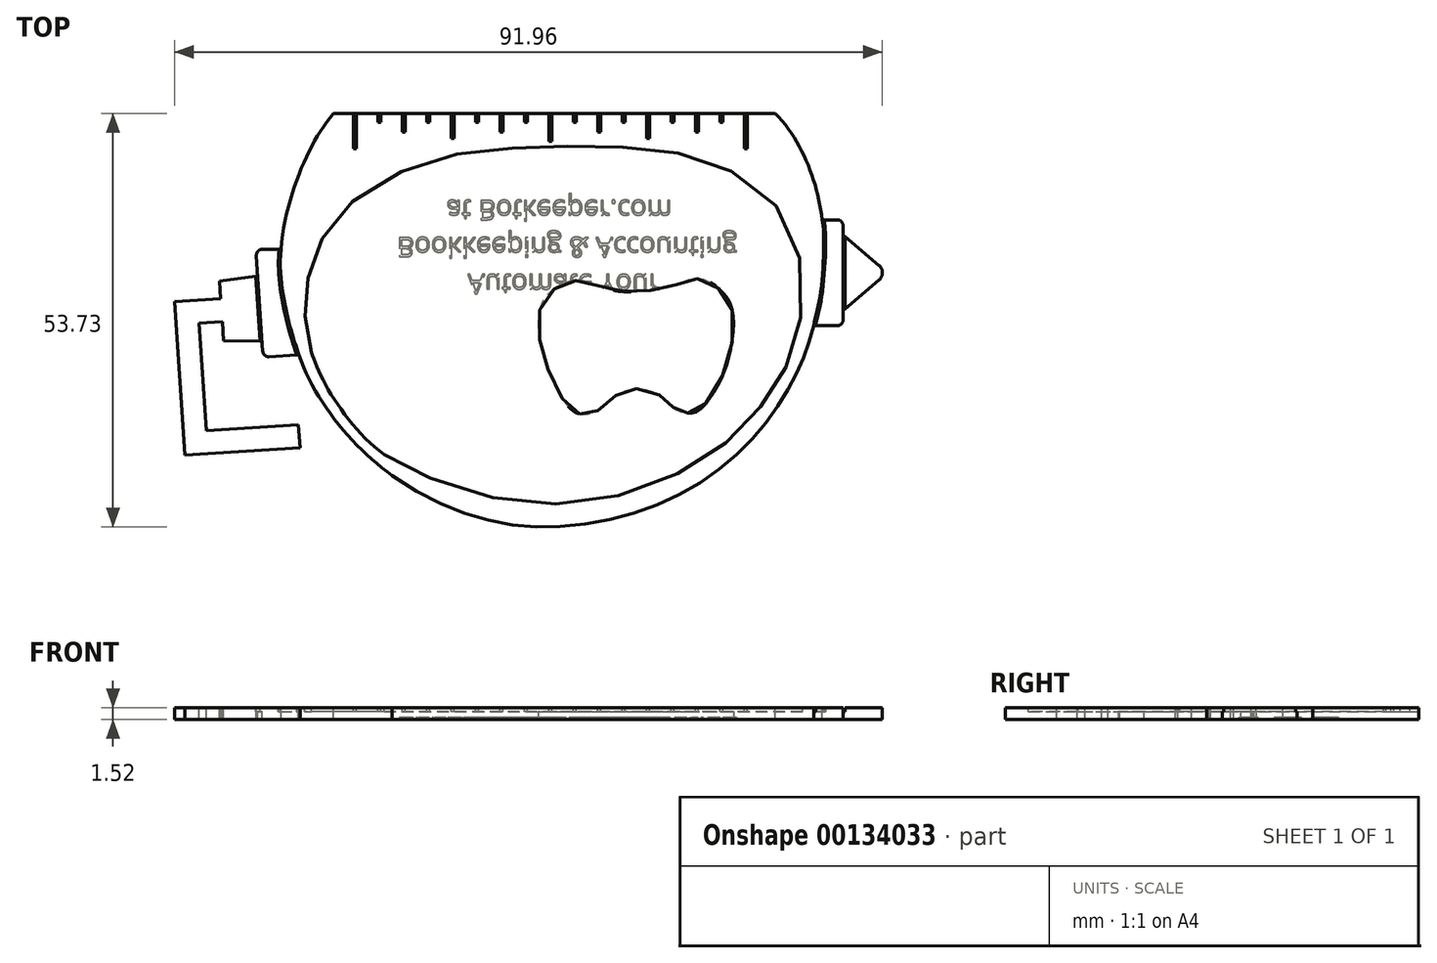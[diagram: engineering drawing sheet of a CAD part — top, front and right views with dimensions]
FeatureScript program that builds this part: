
annotation { "Feature Type Name" : "Feature", "Feature Type Description" : "" }
export const myFeature = defineFeature(function(context is Context, id is Id, definition is map)
    precondition{}
    {
        {
            var Q0;
            Q0=qCreatedBy(makeId("Top.planeOp"),FACE);
            var sketch = newSketch(context, id + "F0", { "sketchPlane" : qUnion([Q0])});
            skLineSegment(sketch, "E0", {"start": v(-32.17, -4.38) * mm, "end": v(25.24, -4.38) * mm});
            skFitSpline(sketch, "E1", {"points": [v(17.6, 42.66) * mm, v(-3.45, 49.33) * mm, v(-23.04, 43.2) * mm, v(-33.77, 31.64) * mm, v(-37.48, 21.94) * mm, v(-38.3, 9.44) * mm, v(-32.1, -4.46) * mm], "startDerivative": vector(-109.73, 76.09) * mm, "endDerivative": vector(66.24, -66.24) * mm});
            skFitSpline(sketch, "E2", {"points": [v(25.23, -4.4) * mm, v(29.6, 3.26) * mm, v(32.13, 15.9) * mm, v(29.75, 26.97) * mm], "startDerivative": vector(17.83, 21.76) * mm, "endDerivative": vector(-8.71, 27.13) * mm});
            skLineSegment(sketch, "E3", {"start": v(32.06, 13.27) * mm, "end": v(35.3, 13.27) * mm});
            skLineSegment(sketch, "E4", {"start": v(35.3, 13.27) * mm, "end": v(34.36, 27.3) * mm});
            skLineSegment(sketch, "E5", {"start": v(34.36, 27.3) * mm, "end": v(29.75, 26.97) * mm});
            skLineSegment(sketch, "E6", {"start": v(34.5, 25.2) * mm, "end": v(39.51, 25.18) * mm});
            skLineSegment(sketch, "E7", {"start": v(39.51, 25.18) * mm, "end": v(40.03, 17.43) * mm});
            skLineSegment(sketch, "E8", {"start": v(40.03, 17.43) * mm, "end": v(35.06, 16.75) * mm});
            skLineSegment(sketch, "E9", {"start": v(-37.18, 23.2) * mm, "end": v(-41, 23.2) * mm});
            skLineSegment(sketch, "E10", {"start": v(-41, 23.2) * mm, "end": v(-41, 9.44) * mm});
            skLineSegment(sketch, "E11", {"start": v(-41, 9.44) * mm, "end": v(-38.3, 9.44) * mm});
            skLineSegment(sketch, "E12", {"start": v(-41, 21.2) * mm, "end": v(-46.8, 16.32) * mm});
            skLineSegment(sketch, "E13", {"start": v(-46.8, 16.32) * mm, "end": v(-41, 11.44) * mm});
            skLineSegment(sketch, "E14.bottom", {"start": v(-28.58, 0.2) * mm, "end": v(-28.2, 0.2) * mm});
            skLineSegment(sketch, "E14.top", {"start": v(-28.58, -4.38) * mm, "end": v(-28.2, -4.38) * mm});
            skLineSegment(sketch, "E14.left", {"start": v(-28.58, 0.2) * mm, "end": v(-28.58, -4.38) * mm});
            skLineSegment(sketch, "E14.right", {"start": v(-28.2, 0.2) * mm, "end": v(-28.2, -4.38) * mm});
            skLineSegment(sketch, "E15.bottom", {"start": v(-25.4, -3.21) * mm, "end": v(-25.02, -3.21) * mm});
            skLineSegment(sketch, "E15.top", {"start": v(-25.4, -4.38) * mm, "end": v(-25.02, -4.38) * mm});
            skLineSegment(sketch, "E15.left", {"start": v(-25.4, -3.21) * mm, "end": v(-25.4, -4.38) * mm});
            skLineSegment(sketch, "E15.right", {"start": v(-25.02, -3.21) * mm, "end": v(-25.02, -4.38) * mm});
            skLineSegment(sketch, "E16.bottom", {"start": v(-22.23, -1.94) * mm, "end": v(-21.84, -1.94) * mm});
            skLineSegment(sketch, "E16.top", {"start": v(-22.23, -4.38) * mm, "end": v(-21.84, -4.38) * mm});
            skLineSegment(sketch, "E16.left", {"start": v(-22.23, -1.94) * mm, "end": v(-22.23, -4.38) * mm});
            skLineSegment(sketch, "E16.right", {"start": v(-21.84, -1.94) * mm, "end": v(-21.84, -4.38) * mm});
            skLineSegment(sketch, "E17.bottom", {"start": v(-19.05, -3.21) * mm, "end": v(-18.67, -3.21) * mm});
            skLineSegment(sketch, "E17.top", {"start": v(-19.05, -4.38) * mm, "end": v(-18.67, -4.38) * mm});
            skLineSegment(sketch, "E17.left", {"start": v(-19.05, -3.21) * mm, "end": v(-19.05, -4.38) * mm});
            skLineSegment(sketch, "E17.right", {"start": v(-18.67, -3.21) * mm, "end": v(-18.67, -4.38) * mm});
            skLineSegment(sketch, "E18.bottom", {"start": v(-15.88, -1.14) * mm, "end": v(-15.5, -1.14) * mm});
            skLineSegment(sketch, "E18.top", {"start": v(-15.88, -4.38) * mm, "end": v(-15.5, -4.38) * mm});
            skLineSegment(sketch, "E18.left", {"start": v(-15.88, -1.14) * mm, "end": v(-15.88, -4.38) * mm});
            skLineSegment(sketch, "E18.right", {"start": v(-15.5, -1.14) * mm, "end": v(-15.5, -4.38) * mm});
            skLineSegment(sketch, "E19.bottom", {"start": v(-12.7, -3.21) * mm, "end": v(-12.32, -3.21) * mm});
            skLineSegment(sketch, "E19.top", {"start": v(-12.7, -4.38) * mm, "end": v(-12.32, -4.38) * mm});
            skLineSegment(sketch, "E19.left", {"start": v(-12.7, -3.21) * mm, "end": v(-12.7, -4.38) * mm});
            skLineSegment(sketch, "E19.right", {"start": v(-12.32, -3.21) * mm, "end": v(-12.32, -4.38) * mm});
            skLineSegment(sketch, "E20.bottom", {"start": v(-9.52, -1.94) * mm, "end": v(-9.14, -1.94) * mm});
            skLineSegment(sketch, "E20.top", {"start": v(-9.52, -4.38) * mm, "end": v(-9.14, -4.38) * mm});
            skLineSegment(sketch, "E20.left", {"start": v(-9.52, -1.94) * mm, "end": v(-9.52, -4.38) * mm});
            skLineSegment(sketch, "E20.right", {"start": v(-9.14, -1.94) * mm, "end": v(-9.14, -4.38) * mm});
            skLineSegment(sketch, "E21.bottom", {"start": v(-6.35, -3.21) * mm, "end": v(-5.97, -3.21) * mm});
            skLineSegment(sketch, "E21.top", {"start": v(-6.35, -4.38) * mm, "end": v(-5.97, -4.38) * mm});
            skLineSegment(sketch, "E21.left", {"start": v(-6.35, -3.21) * mm, "end": v(-6.35, -4.38) * mm});
            skLineSegment(sketch, "E21.right", {"start": v(-5.97, -3.21) * mm, "end": v(-5.97, -4.38) * mm});
            skLineSegment(sketch, "E22.bottom", {"start": v(-3.18, -0.76) * mm, "end": v(-2.8, -0.76) * mm});
            skLineSegment(sketch, "E22.top", {"start": v(-3.18, -4.38) * mm, "end": v(-2.8, -4.38) * mm});
            skLineSegment(sketch, "E22.left", {"start": v(-3.18, -0.76) * mm, "end": v(-3.18, -4.38) * mm});
            skLineSegment(sketch, "E22.right", {"start": v(-2.8, -0.76) * mm, "end": v(-2.8, -4.38) * mm});
            skLineSegment(sketch, "E23.bottom", {"start": v(0, -3.21) * mm, "end": v(0.38, -3.21) * mm});
            skLineSegment(sketch, "E23.top", {"start": v(0, -4.38) * mm, "end": v(0.38, -4.38) * mm});
            skLineSegment(sketch, "E23.left", {"start": v(0, -3.21) * mm, "end": v(0, -4.38) * mm});
            skLineSegment(sketch, "E23.right", {"start": v(0.38, -3.21) * mm, "end": v(0.38, -4.38) * mm});
            skLineSegment(sketch, "E24.bottom", {"start": v(3.18, -1.94) * mm, "end": v(3.56, -1.94) * mm});
            skLineSegment(sketch, "E24.top", {"start": v(3.18, -4.38) * mm, "end": v(3.56, -4.38) * mm});
            skLineSegment(sketch, "E24.left", {"start": v(3.18, -1.94) * mm, "end": v(3.18, -4.38) * mm});
            skLineSegment(sketch, "E24.right", {"start": v(3.56, -1.94) * mm, "end": v(3.56, -4.38) * mm});
            skLineSegment(sketch, "E25.bottom", {"start": v(6.35, -3.21) * mm, "end": v(6.73, -3.21) * mm});
            skLineSegment(sketch, "E25.top", {"start": v(6.35, -4.38) * mm, "end": v(6.73, -4.38) * mm});
            skLineSegment(sketch, "E25.left", {"start": v(6.35, -3.21) * mm, "end": v(6.35, -4.38) * mm});
            skLineSegment(sketch, "E25.right", {"start": v(6.73, -3.21) * mm, "end": v(6.73, -4.38) * mm});
            skLineSegment(sketch, "E26.bottom", {"start": v(9.52, -1.14) * mm, "end": v(9.9, -1.14) * mm});
            skLineSegment(sketch, "E26.top", {"start": v(9.52, -4.38) * mm, "end": v(9.9, -4.38) * mm});
            skLineSegment(sketch, "E26.left", {"start": v(9.52, -1.14) * mm, "end": v(9.52, -4.38) * mm});
            skLineSegment(sketch, "E26.right", {"start": v(9.9, -1.14) * mm, "end": v(9.9, -4.38) * mm});
            skLineSegment(sketch, "E27.bottom", {"start": v(12.7, -3.21) * mm, "end": v(13.08, -3.21) * mm});
            skLineSegment(sketch, "E27.top", {"start": v(12.7, -4.38) * mm, "end": v(13.08, -4.38) * mm});
            skLineSegment(sketch, "E27.left", {"start": v(12.7, -3.21) * mm, "end": v(12.7, -4.38) * mm});
            skLineSegment(sketch, "E27.right", {"start": v(13.08, -3.21) * mm, "end": v(13.08, -4.38) * mm});
            skLineSegment(sketch, "E28.bottom", {"start": v(15.88, -1.94) * mm, "end": v(16.26, -1.94) * mm});
            skLineSegment(sketch, "E28.top", {"start": v(15.88, -4.38) * mm, "end": v(16.26, -4.38) * mm});
            skLineSegment(sketch, "E28.left", {"start": v(15.88, -1.94) * mm, "end": v(15.88, -4.38) * mm});
            skLineSegment(sketch, "E28.right", {"start": v(16.26, -1.94) * mm, "end": v(16.26, -4.38) * mm});
            skLineSegment(sketch, "E29.bottom", {"start": v(19.05, -3.21) * mm, "end": v(19.43, -3.21) * mm});
            skLineSegment(sketch, "E29.top", {"start": v(19.05, -4.38) * mm, "end": v(19.43, -4.38) * mm});
            skLineSegment(sketch, "E29.left", {"start": v(19.05, -3.21) * mm, "end": v(19.05, -4.38) * mm});
            skLineSegment(sketch, "E29.right", {"start": v(19.43, -3.21) * mm, "end": v(19.43, -4.38) * mm});
            skLineSegment(sketch, "E30.bottom", {"start": v(22.23, 0.2) * mm, "end": v(22.6, 0.2) * mm});
            skLineSegment(sketch, "E30.top", {"start": v(22.23, -4.38) * mm, "end": v(22.6, -4.38) * mm});
            skLineSegment(sketch, "E30.left", {"start": v(22.23, 0.2) * mm, "end": v(22.23, -4.38) * mm});
            skLineSegment(sketch, "E30.right", {"start": v(22.6, 0.2) * mm, "end": v(22.6, -4.38) * mm});
            skFitSpline(sketch, "E31", {"points": [v(29.75, 26.97) * mm, v(17.6, 42.66) * mm], "startDerivative": vector(-6.37, 18.37) * mm, "endDerivative": vector(-15.48, 11.18) * mm});
            skSolve(sketch);
        }
        {
            var Q0;
            {var subQ0=sQuery(id+"F0.wireOp",EDGE,"E12");Q0=makeQuery(id+"F0.imprint","IMPRINT",FACE,{"disambiguationData":[TD([[makeQuery(id+"F0.imprint","IMPRINT",EDGE,{"derivedFrom":subQ0}),1.0]])]});}
            var Q1;
            {var subQ0=sQuery(id+"F0.wireOp",EDGE,"E9");Q1=makeQuery(id+"F0.imprint","IMPRINT",FACE,{"disambiguationData":[TD([[makeQuery(id+"F0.imprint","IMPRINT",EDGE,{"derivedFrom":subQ0}),1.0]])]});}
            var Q2;
            {var subQ4=sQuery(id+"F0.wireOp",EDGE,"E0");Q2=makeQuery(id+"F0.imprint","IMPRINT",FACE,{"disambiguationData":[TD([[makeQuery(id+"F0.imprint","IMPRINT",EDGE,{"derivedFrom":subQ4}),1.0]])]});}
            var Q3;
            {var subQ3=sQuery(id+"F0.wireOp",EDGE,"E3");Q3=makeQuery(id+"F0.imprint","IMPRINT",FACE,{"disambiguationData":[TD([[makeQuery(id+"F0.imprint","IMPRINT",EDGE,{"derivedFrom":subQ3}),1.0]])]});}
            var Q4;
            {var subQ0=sQuery(id+"F0.wireOp",EDGE,"E6");Q4=makeQuery(id+"F0.imprint","IMPRINT",FACE,{"disambiguationData":[TD([[makeQuery(id+"F0.imprint","IMPRINT",EDGE,{"derivedFrom":subQ0}),-1.0]])]});}
            var Q5;
            Q5=makeQuery(id+"F0.imprint","IMPRINT",FACE,{"disambiguationData":[TD([[makeQuery(id+"F0.imprint","IMPRINT",EDGE,{"derivedFrom":sQuery(id+"F0.wireOp",EDGE,"E14.bottom")}),-1.0]])]});
            var Q6;
            Q6=makeQuery(id+"F0.imprint","IMPRINT",FACE,{"disambiguationData":[TD([[makeQuery(id+"F0.imprint","IMPRINT",EDGE,{"derivedFrom":sQuery(id+"F0.wireOp",EDGE,"E15.bottom")}),-1.0]])]});
            var Q7;
            Q7=makeQuery(id+"F0.imprint","IMPRINT",FACE,{"disambiguationData":[TD([[makeQuery(id+"F0.imprint","IMPRINT",EDGE,{"derivedFrom":sQuery(id+"F0.wireOp",EDGE,"E16.bottom")}),-1.0]])]});
            var Q8;
            Q8=makeQuery(id+"F0.imprint","IMPRINT",FACE,{"disambiguationData":[TD([[makeQuery(id+"F0.imprint","IMPRINT",EDGE,{"derivedFrom":sQuery(id+"F0.wireOp",EDGE,"E17.bottom")}),-1.0]])]});
            var Q9;
            Q9=makeQuery(id+"F0.imprint","IMPRINT",FACE,{"disambiguationData":[TD([[makeQuery(id+"F0.imprint","IMPRINT",EDGE,{"derivedFrom":sQuery(id+"F0.wireOp",EDGE,"E18.bottom")}),-1.0]])]});
            var Q10;
            Q10=makeQuery(id+"F0.imprint","IMPRINT",FACE,{"disambiguationData":[TD([[makeQuery(id+"F0.imprint","IMPRINT",EDGE,{"derivedFrom":sQuery(id+"F0.wireOp",EDGE,"E19.bottom")}),-1.0]])]});
            var Q11;
            Q11=makeQuery(id+"F0.imprint","IMPRINT",FACE,{"disambiguationData":[TD([[makeQuery(id+"F0.imprint","IMPRINT",EDGE,{"derivedFrom":sQuery(id+"F0.wireOp",EDGE,"E20.bottom")}),-1.0]])]});
            var Q12;
            Q12=makeQuery(id+"F0.imprint","IMPRINT",FACE,{"disambiguationData":[TD([[makeQuery(id+"F0.imprint","IMPRINT",EDGE,{"derivedFrom":sQuery(id+"F0.wireOp",EDGE,"E21.bottom")}),-1.0]])]});
            var Q13;
            Q13=makeQuery(id+"F0.imprint","IMPRINT",FACE,{"disambiguationData":[TD([[makeQuery(id+"F0.imprint","IMPRINT",EDGE,{"derivedFrom":sQuery(id+"F0.wireOp",EDGE,"E22.bottom")}),-1.0]])]});
            var Q14;
            Q14=makeQuery(id+"F0.imprint","IMPRINT",FACE,{"disambiguationData":[TD([[makeQuery(id+"F0.imprint","IMPRINT",EDGE,{"derivedFrom":sQuery(id+"F0.wireOp",EDGE,"E23.bottom")}),-1.0]])]});
            var Q15;
            Q15=makeQuery(id+"F0.imprint","IMPRINT",FACE,{"disambiguationData":[TD([[makeQuery(id+"F0.imprint","IMPRINT",EDGE,{"derivedFrom":sQuery(id+"F0.wireOp",EDGE,"E24.bottom")}),-1.0]])]});
            var Q16;
            Q16=makeQuery(id+"F0.imprint","IMPRINT",FACE,{"disambiguationData":[TD([[makeQuery(id+"F0.imprint","IMPRINT",EDGE,{"derivedFrom":sQuery(id+"F0.wireOp",EDGE,"E25.bottom")}),-1.0]])]});
            var Q17;
            Q17=makeQuery(id+"F0.imprint","IMPRINT",FACE,{"disambiguationData":[TD([[makeQuery(id+"F0.imprint","IMPRINT",EDGE,{"derivedFrom":sQuery(id+"F0.wireOp",EDGE,"E26.bottom")}),-1.0]])]});
            var Q18;
            Q18=makeQuery(id+"F0.imprint","IMPRINT",FACE,{"disambiguationData":[TD([[makeQuery(id+"F0.imprint","IMPRINT",EDGE,{"derivedFrom":sQuery(id+"F0.wireOp",EDGE,"E27.bottom")}),-1.0]])]});
            var Q19;
            Q19=makeQuery(id+"F0.imprint","IMPRINT",FACE,{"disambiguationData":[TD([[makeQuery(id+"F0.imprint","IMPRINT",EDGE,{"derivedFrom":sQuery(id+"F0.wireOp",EDGE,"E28.bottom")}),-1.0]])]});
            var Q20;
            Q20=makeQuery(id+"F0.imprint","IMPRINT",FACE,{"disambiguationData":[TD([[makeQuery(id+"F0.imprint","IMPRINT",EDGE,{"derivedFrom":sQuery(id+"F0.wireOp",EDGE,"E29.bottom")}),-1.0]])]});
            var Q21;
            Q21=makeQuery(id+"F0.imprint","IMPRINT",FACE,{"disambiguationData":[TD([[makeQuery(id+"F0.imprint","IMPRINT",EDGE,{"derivedFrom":sQuery(id+"F0.wireOp",EDGE,"E30.bottom")}),-1.0]])]});
            extrude(context, id + "F1", {"entities" : qUnion([Q0, Q1, Q2, Q3, Q4, Q5, Q6, Q7, Q8, Q9, Q10, Q11, Q12, Q13, Q14, Q15, Q16, Q17, Q18, Q19, Q20, Q21]), "oppositeDirection" : true, "depth" : 1.52 * mm});
        }
        {
            var Q0;
            Q0=makeQuery(id+"F0.imprint","IMPRINT",FACE,{"disambiguationData":[TD([[makeQuery(id+"F0.imprint","IMPRINT",EDGE,{"derivedFrom":sQuery(id+"F0.wireOp",EDGE,"E14.bottom")}),1.0]])]});
            var sketch = newSketch(context, id + "F2", { "sketchPlane" : qUnion([Q0])});
            skCircle(sketch, "E32", {"center": v(-14.4, 25.5) * mm, "radius": 6.39 * mm, "construction": true});
            skPoint(sketch, "E32.first.point", {"position": v(-19.79, 28.93) * mm});
            skPoint(sketch, "E32.second.point", {"position": v(-8.02, 25.7) * mm});
            skPoint(sketch, "E32.third.point", {"position": v(-14.79, 19.13) * mm});
            skCircle(sketch, "E33", {"center": v(-14.4, 25.5) * mm, "radius": 8.66 * mm, "construction": true});
            skPoint(sketch, "E33.first.point", {"position": v(-17.82, 33.46) * mm});
            skPoint(sketch, "E33.second.point", {"position": v(-5.87, 27.02) * mm});
            skPoint(sketch, "E33.third.point", {"position": v(-19.38, 18.42) * mm});
            skArc(sketch, "E34", {"start": v(13.5, 25.47) * mm, "mid": v(7.55, 27.76) * mm, "end": v(1.85, 24.89) * mm});
            skArc(sketch, "E35", {"start": v(15.13, 27.13) * mm, "mid": v(7.4, 30.06) * mm, "end": v(-0.06, 26.51) * mm});
            skArc(sketch, "E36", {"start": v(-0.06, 26.51) * mm, "mid": v(0.07, 24.73) * mm, "end": v(1.85, 24.89) * mm});
            skArc(sketch, "E37", {"start": v(13.5, 25.47) * mm, "mid": v(15.16, 25.47) * mm, "end": v(15.13, 27.13) * mm});
            skArc(sketch, "E38", {"start": v(-11.18, 12.88) * mm, "mid": v(-2.27, 11.02) * mm, "end": v(5.19, 16.23) * mm});
            skArc(sketch, "E39", {"start": v(-12.5, 11) * mm, "mid": v(-1.88, 8.77) * mm, "end": v(7.06, 14.9) * mm});
            skArc(sketch, "E40", {"start": v(-11.18, 12.88) * mm, "mid": v(-12.77, 12.6) * mm, "end": v(-12.5, 11) * mm});
            skLineSegment(sketch, "E41", {"start": v(5.19, 16.23) * mm, "end": v(4.3, 16.9) * mm});
            skLineSegment(sketch, "E42", {"start": v(7.06, 14.9) * mm, "end": v(7.66, 14.46) * mm});
            skLineSegment(sketch, "E43", {"start": v(5.65, 18.78) * mm, "end": v(9.06, 16.4) * mm});
            skArc(sketch, "E44", {"start": v(5.65, 18.78) * mm, "mid": v(4.05, 18.51) * mm, "end": v(4.3, 16.9) * mm});
            skArc(sketch, "E45", {"start": v(7.66, 14.46) * mm, "mid": v(9.34, 14.72) * mm, "end": v(9.06, 16.4) * mm});
            skPoint(sketch, "E46.first.point", {"position": v(-14.74, 32.09) * mm});
            skPoint(sketch, "E46.second.point", {"position": v(-20.28, 23.46) * mm});
            skPoint(sketch, "E46.third.point", {"position": v(-8.39, 22.95) * mm});
            skSolve(sketch);
        }
        {
            var Q0;
            Q0 = qSketchRegion(id + "F2", true);
            extrude(context, id + "F3", {"entities" : qUnion([Q0]), "operationType" : NewBodyOperationType.REMOVE, "oppositeDirection" : true, "depth" : 0.5 * mm});
        }
        {
            var Q0;
            Q0=makeQuery(id+"F0.imprint","IMPRINT",FACE,{"disambiguationData":[TD([[makeQuery(id+"F0.imprint","IMPRINT",EDGE,{"derivedFrom":sQuery(id+"F0.wireOp",EDGE,"E14.bottom")}),-1.0]])]});
            var Q1;
            Q1=makeQuery(id+"F0.imprint","IMPRINT",FACE,{"disambiguationData":[TD([[makeQuery(id+"F0.imprint","IMPRINT",EDGE,{"derivedFrom":sQuery(id+"F0.wireOp",EDGE,"E15.bottom")}),-1.0]])]});
            var Q2;
            Q2=makeQuery(id+"F0.imprint","IMPRINT",FACE,{"disambiguationData":[TD([[makeQuery(id+"F0.imprint","IMPRINT",EDGE,{"derivedFrom":sQuery(id+"F0.wireOp",EDGE,"E16.bottom")}),-1.0]])]});
            var Q3;
            Q3=makeQuery(id+"F0.imprint","IMPRINT",FACE,{"disambiguationData":[TD([[makeQuery(id+"F0.imprint","IMPRINT",EDGE,{"derivedFrom":sQuery(id+"F0.wireOp",EDGE,"E18.bottom")}),-1.0]])]});
            var Q4;
            Q4=makeQuery(id+"F0.imprint","IMPRINT",FACE,{"disambiguationData":[TD([[makeQuery(id+"F0.imprint","IMPRINT",EDGE,{"derivedFrom":sQuery(id+"F0.wireOp",EDGE,"E17.bottom")}),-1.0]])]});
            var Q5;
            Q5=makeQuery(id+"F0.imprint","IMPRINT",FACE,{"disambiguationData":[TD([[makeQuery(id+"F0.imprint","IMPRINT",EDGE,{"derivedFrom":sQuery(id+"F0.wireOp",EDGE,"E19.bottom")}),-1.0]])]});
            var Q6;
            Q6=makeQuery(id+"F0.imprint","IMPRINT",FACE,{"disambiguationData":[TD([[makeQuery(id+"F0.imprint","IMPRINT",EDGE,{"derivedFrom":sQuery(id+"F0.wireOp",EDGE,"E20.bottom")}),-1.0]])]});
            var Q7;
            Q7=makeQuery(id+"F0.imprint","IMPRINT",FACE,{"disambiguationData":[TD([[makeQuery(id+"F0.imprint","IMPRINT",EDGE,{"derivedFrom":sQuery(id+"F0.wireOp",EDGE,"E21.bottom")}),-1.0]])]});
            var Q8;
            Q8=makeQuery(id+"F0.imprint","IMPRINT",FACE,{"disambiguationData":[TD([[makeQuery(id+"F0.imprint","IMPRINT",EDGE,{"derivedFrom":sQuery(id+"F0.wireOp",EDGE,"E22.bottom")}),-1.0]])]});
            var Q9;
            Q9=makeQuery(id+"F0.imprint","IMPRINT",FACE,{"disambiguationData":[TD([[makeQuery(id+"F0.imprint","IMPRINT",EDGE,{"derivedFrom":sQuery(id+"F0.wireOp",EDGE,"E23.bottom")}),-1.0]])]});
            var Q10;
            Q10=makeQuery(id+"F0.imprint","IMPRINT",FACE,{"disambiguationData":[TD([[makeQuery(id+"F0.imprint","IMPRINT",EDGE,{"derivedFrom":sQuery(id+"F0.wireOp",EDGE,"E24.bottom")}),-1.0]])]});
            var Q11;
            Q11=makeQuery(id+"F0.imprint","IMPRINT",FACE,{"disambiguationData":[TD([[makeQuery(id+"F0.imprint","IMPRINT",EDGE,{"derivedFrom":sQuery(id+"F0.wireOp",EDGE,"E25.bottom")}),-1.0]])]});
            var Q12;
            Q12=makeQuery(id+"F0.imprint","IMPRINT",FACE,{"disambiguationData":[TD([[makeQuery(id+"F0.imprint","IMPRINT",EDGE,{"derivedFrom":sQuery(id+"F0.wireOp",EDGE,"E26.bottom")}),-1.0]])]});
            var Q13;
            Q13=makeQuery(id+"F0.imprint","IMPRINT",FACE,{"disambiguationData":[TD([[makeQuery(id+"F0.imprint","IMPRINT",EDGE,{"derivedFrom":sQuery(id+"F0.wireOp",EDGE,"E27.bottom")}),-1.0]])]});
            var Q14;
            Q14=makeQuery(id+"F0.imprint","IMPRINT",FACE,{"disambiguationData":[TD([[makeQuery(id+"F0.imprint","IMPRINT",EDGE,{"derivedFrom":sQuery(id+"F0.wireOp",EDGE,"E28.bottom")}),-1.0]])]});
            var Q15;
            Q15=makeQuery(id+"F0.imprint","IMPRINT",FACE,{"disambiguationData":[TD([[makeQuery(id+"F0.imprint","IMPRINT",EDGE,{"derivedFrom":sQuery(id+"F0.wireOp",EDGE,"E29.bottom")}),-1.0]])]});
            var Q16;
            Q16=makeQuery(id+"F0.imprint","IMPRINT",FACE,{"disambiguationData":[TD([[makeQuery(id+"F0.imprint","IMPRINT",EDGE,{"derivedFrom":sQuery(id+"F0.wireOp",EDGE,"E30.bottom")}),-1.0]])]});
            extrude(context, id + "F4", {"entities" : qUnion([Q0, Q1, Q2, Q3, Q4, Q5, Q6, Q7, Q8, Q9, Q10, Q11, Q12, Q13, Q14, Q15, Q16]), "operationType" : NewBodyOperationType.REMOVE, "oppositeDirection" : true, "depth" : 0.5 * mm});
        }
        {
            var Q0;
            {var subQ0=sQuery(id+"F0.wireOp",EDGE,"E31");var subQ1=sQuery(id+"F0.wireOp",EDGE,"E13");var subQ2=sQuery(id+"F0.wireOp",EDGE,"E12");var subQ3=sQuery(id+"F0.wireOp",EDGE,"E11");var subQ4=sQuery(id+"F0.wireOp",EDGE,"E10");var subQ5=sQuery(id+"F0.wireOp",EDGE,"E9");var subQ6=sQuery(id+"F0.wireOp",EDGE,"E8");var subQ7=sQuery(id+"F0.wireOp",EDGE,"E2");var subQ8=sQuery(id+"F0.wireOp",EDGE,"E1");var subQ9=sQuery(id+"F0.wireOp",EDGE,"E0");var subQ10=sQuery(id+"F0.wireOp",EDGE,"E30.top");var subQ11=sQuery(id+"F0.wireOp",EDGE,"E29.top");var subQ12=sQuery(id+"F0.wireOp",EDGE,"E28.top");var subQ13=sQuery(id+"F0.wireOp",EDGE,"E27.top");var subQ14=sQuery(id+"F0.wireOp",EDGE,"E26.top");var subQ15=sQuery(id+"F0.wireOp",EDGE,"E25.top");var subQ16=sQuery(id+"F0.wireOp",EDGE,"E24.top");var subQ17=sQuery(id+"F0.wireOp",EDGE,"E23.top");var subQ18=sQuery(id+"F0.wireOp",EDGE,"E22.top");var subQ19=sQuery(id+"F0.wireOp",EDGE,"E21.top");var subQ20=sQuery(id+"F0.wireOp",EDGE,"E20.top");var subQ21=sQuery(id+"F0.wireOp",EDGE,"E19.top");var subQ22=sQuery(id+"F0.wireOp",EDGE,"E18.top");var subQ23=sQuery(id+"F0.wireOp",EDGE,"E17.top");var subQ24=sQuery(id+"F0.wireOp",EDGE,"E16.top");var subQ25=sQuery(id+"F0.wireOp",EDGE,"E15.top");var subQ26=sQuery(id+"F0.wireOp",EDGE,"E14.top");var subQ27=sQuery(id+"F0.wireOp",EDGE,"E3");var subQ28=sQuery(id+"F0.wireOp",EDGE,"E4");var subQ29=sQuery(id+"F0.wireOp",EDGE,"E5");var subQ30=sQuery(id+"F0.wireOp",EDGE,"E6");var subQ31=sQuery(id+"F0.wireOp",EDGE,"E7");Q0=makeQuery(id+"F3.boolean.opBoolean","SPLIT",FACE,{"disambiguationData":[TD([makeQuery(id+"F1.opExtrude","SWEPT_FACE",FACE,{"disambiguationData":[OSD([subQ7])]})])],"derivedFrom":makeQuery(id+"F1.opExtrude","CAP_FACE",FACE,{"disambiguationData":[OSD([subQ9,subQ8,subQ7,subQ27,subQ28,subQ29,subQ30,subQ31,subQ6,subQ5,subQ4,subQ3,subQ2,subQ1,subQ26,subQ25,subQ24,subQ23,subQ22,subQ21,subQ20,subQ19,subQ18,subQ17,subQ16,subQ15,subQ14,subQ13,subQ12,subQ11,subQ10,subQ0])],"isStart":true})});}
            var sketch = newSketch(context, id + "F5", { "sketchPlane" : qUnion([Q0])});
            skFitSpline(sketch, "E47", {"points": [v(18.63, 39.92) * mm, v(6.25, 45.15) * mm, v(-9.8, 45.73) * mm, v(-23.9, 39.86) * mm, v(-31.2, 32.51) * mm, v(-35.12, 23.96) * mm, v(-34.08, 10.46) * mm, v(-24.53, 2.23) * mm, v(-12.25, 0) * mm, v(0.1, 0.07) * mm, v(12.6, 1.76) * mm, v(23.95, 8.14) * mm, v(28.06, 15.22) * mm, v(28.98, 21.31) * mm, v(28.06, 26.68) * mm], "startDerivative": vector(-92.5, 61.42) * mm, "endDerivative": vector(-25.36, 109.51) * mm});
            skFitSpline(sketch, "E48.0", {"points": [v(18.77, 40.14) * mm, v(17.8, 40.79) * mm, v(15.7, 41.93) * mm, v(12.18, 43.46) * mm, v(9.3, 44.53) * mm, v(6.3, 45.44) * mm, v(3.3, 46.1) * mm, v(0.33, 46.51) * mm, v(-2.63, 46.68) * mm, v(-5.58, 46.59) * mm, v(-8.52, 46.25) * mm, v(-11.45, 45.66) * mm, v(-15.31, 44.56) * mm, v(-19, 43.05) * mm, v(-22.32, 41.23) * mm, v(-24.57, 39.74) * mm, v(-26.56, 38.15) * mm, v(-28.3, 36.48) * mm, v(-29.85, 34.74) * mm, v(-31.22, 32.96) * mm, v(-32.46, 31.13) * mm, v(-33.55, 29.22) * mm, v(-34.48, 27.16) * mm, v(-35.09, 25.27) * mm, v(-35.47, 23.62) * mm, v(-35.77, 21.88) * mm, v(-36, 19.58) * mm, v(-35.96, 16.72) * mm, v(-35.57, 13.89) * mm, v(-34.9, 11.64) * mm, v(-34.15, 9.97) * mm, v(-33.23, 8.4) * mm, v(-31.82, 6.64) * mm, v(-29.8, 4.84) * mm, v(-27.53, 3.34) * mm, v(-25.1, 2.14) * mm, v(-22.6, 1.23) * mm, v(-20.05, 0.59) * mm, v(-17.46, 0.15) * mm, v(-14.86, -0.12) * mm, v(-12.26, -0.27) * mm, v(-9.66, -0.35) * mm, v(-7.08, -0.37) * mm, v(-4.5, -0.33) * mm, v(-1.91, -0.26) * mm, v(0.66, -0.16) * mm, v(3.24, -0.04) * mm, v(5.82, 0.17) * mm, v(8.42, 0.5) * mm, v(10.6, 0.94) * mm, v(12.34, 1.4) * mm, v(14.1, 1.95) * mm, v(16.28, 2.8) * mm, v(18.8, 4.03) * mm, v(21.13, 5.45) * mm, v(22.86, 6.76) * mm, v(24.07, 7.89) * mm, v(25.15, 9.05) * mm, v(26.27, 10.56) * mm, v(27.3, 12.43) * mm, v(28.06, 14.32) * mm, v(28.64, 16.2) * mm, v(29.04, 18.05) * mm, v(29.25, 19.87) * mm, v(29.25, 21.65) * mm, v(29.05, 23.36) * mm, v(28.71, 25.04) * mm, v(28.44, 26.17) * mm, v(28.31, 26.74) * mm]});
            skFitSpline(sketch, "E49", {"points": [v(16.65, 38.55) * mm, v(8.91, 42.59) * mm, v(-6.12, 44.42) * mm, v(-21.45, 39.35) * mm, v(-32.5, 24.95) * mm, v(-28.84, 9.66) * mm, v(-16.86, 4.32) * mm, v(-0.56, 3.68) * mm, v(17, 7.95) * mm, v(23.1, 12.81) * mm, v(25.48, 18.24) * mm, v(25.01, 25.93) * mm], "startDerivative": vector(-89.1, 67.64) * mm, "endDerivative": vector(-21.26, 103.14) * mm});
            skFitSpline(sketch, "E50.0", {"points": [v(16.5, 38.35) * mm, v(15.57, 39.05) * mm, v(14.17, 40) * mm, v(12.11, 41.08) * mm, v(10.43, 41.8) * mm, v(8.57, 42.45) * mm, v(6.5, 43.03) * mm, v(4.26, 43.5) * mm, v(1.9, 43.88) * mm, v(-0.56, 44.14) * mm, v(-3.05, 44.25) * mm, v(-5.54, 44.22) * mm, v(-8, 44.02) * mm, v(-10.4, 43.65) * mm, v(-13.53, 42.92) * mm, v(-16.58, 41.8) * mm, v(-19.53, 40.28) * mm, v(-22.41, 38.47) * mm, v(-25.89, 35.67) * mm, v(-28.83, 32.27) * mm, v(-30.65, 29.28) * mm, v(-31.71, 26.91) * mm, v(-32.4, 24.45) * mm, v(-32.7, 21.9) * mm, v(-32.63, 19.33) * mm, v(-32.22, 16.82) * mm, v(-31.48, 14.43) * mm, v(-30.45, 12.24) * mm, v(-29.16, 10.32) * mm, v(-27.63, 8.74) * mm, v(-25.88, 7.48) * mm, v(-23.96, 6.48) * mm, v(-21.88, 5.71) * mm, v(-19.7, 5.12) * mm, v(-17.43, 4.66) * mm, v(-15.13, 4.28) * mm, v(-12.8, 3.99) * mm, v(-9.62, 3.7) * mm, v(-5.53, 3.59) * mm, v(-0.35, 3.88) * mm, v(5.16, 4.65) * mm, v(9.64, 5.63) * mm, v(12.93, 6.6) * mm, v(15.2, 7.4) * mm, v(17.19, 8.29) * mm, v(18.87, 9.23) * mm, v(20.3, 10.24) * mm, v(21.5, 11.3) * mm, v(22.51, 12.43) * mm, v(23.4, 13.6) * mm, v(24.13, 14.85) * mm, v(24.72, 16.17) * mm, v(25.07, 17.35) * mm, v(25.25, 18.36) * mm, v(25.37, 19.41) * mm, v(25.4, 20.8) * mm, v(25.27, 23.1) * mm, v(24.99, 24.8) * mm, v(24.77, 25.88) * mm]});
            skFitSpline(sketch, "E51", {"points": [v(18.55, 40.28) * mm, v(28.31, 26.74) * mm], "startDerivative": vector(16.28, -10.65) * mm, "endDerivative": vector(1.29, -6.83) * mm});
            skFitSpline(sketch, "E52", {"points": [v(18.63, 39.92) * mm, v(28.06, 26.68) * mm], "startDerivative": vector(14.82, -10.54) * mm, "endDerivative": vector(2.36, -8.87) * mm});
            skFitSpline(sketch, "E53", {"points": [v(16.65, 38.55) * mm, v(25.01, 25.93) * mm], "startDerivative": vector(12.95, -9.36) * mm, "endDerivative": vector(3.32, -15.64) * mm});
            skFitSpline(sketch, "E54", {"points": [v(16.1, 38.64) * mm, v(24.77, 25.88) * mm], "startDerivative": vector(14.37, -10.65) * mm, "endDerivative": vector(3.62, -15.46) * mm});
            skSolve(sketch);
        }
        {
            var Q0;
            Q0 = qSketchRegion(id + "F5", true);
            var Q1;
            Q1=makeQuery(id+"F5.imprint","IMPRINT",FACE,{"disambiguationData":[TD([[makeQuery(id+"F5.imprint","IMPRINT",EDGE,{"derivedFrom":sQuery(id+"F5.wireOp",EDGE,"E49")}),1.0]])]});
            extrude(context, id + "F6", {"entities" : qUnion([Q0, Q1]), "operationType" : NewBodyOperationType.REMOVE, "oppositeDirection" : true, "depth" : 0.5 * mm});
        }
        {
            var Q0;
            {var subQ1=sQuery(id+"F0.wireOp",EDGE,"E9");Q0=makeQuery(id+"F0.imprint","IMPRINT",FACE,{"disambiguationData":[TD([[makeQuery(id+"F0.imprint","IMPRINT",EDGE,{"derivedFrom":subQ1}),1.0]])]});}
            var sketch = newSketch(context, id + "F7", { "sketchPlane" : qUnion([Q0])});
            skFitSpline(sketch, "E55", {"points": [v(-37.18, 23.2) * mm, v(-38.04, 19.13) * mm, v(-38.48, 12.2) * mm, v(-38.3, 9.44) * mm], "startDerivative": vector(-2.28, -11.85) * mm, "endDerivative": vector(1.36, -9.07) * mm});
            skLineSegment(sketch, "E56", {"start": v(-37.18, 23.2) * mm, "end": v(-37.43, 23.2) * mm});
            skLineSegment(sketch, "E57", {"start": v(-38.3, 9.44) * mm, "end": v(-38.55, 9.44) * mm});
            skFitSpline(sketch, "E58", {"points": [v(-38.55, 9.44) * mm, v(-38.72, 12.21) * mm, v(-38.25, 19.15) * mm, v(-37.43, 23.2) * mm], "startDerivative": vector(-0.96, 8.99) * mm, "endDerivative": vector(2.28, 11.38) * mm});
            skLineSegment(sketch, "E59", {"start": v(-41, 21.2) * mm, "end": v(-41, 11.44) * mm});
            skLineSegment(sketch, "E60", {"start": v(-41, 11.44) * mm, "end": v(-41.23, 11.53) * mm});
            skLineSegment(sketch, "E61", {"start": v(-41, 21.2) * mm, "end": v(-41.23, 21.1) * mm});
            skLineSegment(sketch, "E62", {"start": v(-41.23, 21.1) * mm, "end": v(-41.23, 11.53) * mm});
            skSolve(sketch);
        }
        {
            var Q0;
            Q0 = qSketchRegion(id + "F7", true);
            extrude(context, id + "F8", {"entities" : qUnion([Q0]), "operationType" : NewBodyOperationType.REMOVE, "oppositeDirection" : true, "depth" : 0.5 * mm});
        }
        {
            var Q0;
            {var subQ0=sQuery(id+"F0.wireOp",EDGE,"E6");Q0=makeQuery(id+"F0.imprint","IMPRINT",FACE,{"disambiguationData":[TD([[makeQuery(id+"F0.imprint","IMPRINT",EDGE,{"derivedFrom":subQ0}),-1.0]])]});}
            var sketch = newSketch(context, id + "F9", { "sketchPlane" : qUnion([Q0])});
            skFitSpline(sketch, "E63", {"points": [v(32.06, 13.27) * mm, v(31.62, 20.06) * mm, v(30.57, 24.31) * mm, v(29.75, 26.97) * mm], "startDerivative": vector(1.72, 17.72) * mm, "endDerivative": vector(-3.13, 9.56) * mm});
            skLineSegment(sketch, "E64", {"start": v(29.75, 26.97) * mm, "end": v(30, 27) * mm});
            skLineSegment(sketch, "E65", {"start": v(32.06, 13.27) * mm, "end": v(32.3, 13.24) * mm});
            skFitSpline(sketch, "E66", {"points": [v(32.3, 13.24) * mm, v(32.36, 15.9) * mm, v(31.87, 20.06) * mm, v(30.83, 24.37) * mm, v(30, 27) * mm], "startDerivative": vector(0.8, 11.73) * mm, "endDerivative": vector(-4.03, 10.89) * mm});
            skLineSegment(sketch, "E67", {"start": v(34.5, 25.2) * mm, "end": v(35.06, 16.75) * mm});
            skLineSegment(sketch, "E68", {"start": v(35.06, 16.75) * mm, "end": v(35.31, 16.77) * mm});
            skLineSegment(sketch, "E69", {"start": v(34.5, 25.2) * mm, "end": v(34.75, 25.2) * mm});
            skLineSegment(sketch, "E70", {"start": v(34.75, 25.2) * mm, "end": v(35.31, 16.77) * mm});
            skSolve(sketch);
        }
        {
            var Q0;
            Q0 = qSketchRegion(id + "F9", true);
            extrude(context, id + "F10", {"entities" : qUnion([Q0]), "operationType" : NewBodyOperationType.REMOVE, "oppositeDirection" : true, "depth" : 0.5 * mm});
        }
        {
            var Q0;
            Q0=makeQuery(id+"F1.opExtrude","SWEPT_EDGE",EDGE,{"disambiguationData":[OSD([sQuery(id+"F0.wireOp",EDGE,"E12"),sQuery(id+"F0.wireOp",EDGE,"E13")])]});
            fillet(context, id + "F11", {"entities" : qUnion([Q0]), "radius" : 1.27 * mm, "tangentPropagation" : true, "allowEdgeOverflow" : false});
        }
        {
            var Q0;
            Q0=makeQuery(id+"F1.opExtrude","SWEPT_EDGE",EDGE,{"disambiguationData":[OSD([sQuery(id+"F0.wireOp",EDGE,"E9"),sQuery(id+"F0.wireOp",EDGE,"E10")])]});
            var Q1;
            Q1=makeQuery(id+"F1.opExtrude","SWEPT_EDGE",EDGE,{"disambiguationData":[OSD([sQuery(id+"F0.wireOp",EDGE,"E10"),sQuery(id+"F0.wireOp",EDGE,"E11")])]});
            var Q2;
            Q2=makeQuery(id+"F1.opExtrude","SWEPT_EDGE",EDGE,{"disambiguationData":[OSD([sQuery(id+"F0.wireOp",EDGE,"E3"),sQuery(id+"F0.wireOp",EDGE,"E4")])]});
            var Q3;
            Q3=makeQuery(id+"F1.opExtrude","SWEPT_EDGE",EDGE,{"disambiguationData":[OSD([sQuery(id+"F0.wireOp",EDGE,"E4"),sQuery(id+"F0.wireOp",EDGE,"E5")])]});
            fillet(context, id + "F12", {"entities" : qUnion([Q0, Q1, Q2, Q3]), "radius" : 0.76 * mm, "tangentPropagation" : true, "allowEdgeOverflow" : false});
        }
        {
            var Q0;
            Q0=makeQuery(id+"F1.opExtrude","SWEPT_BODY",BODY,{"disambiguationData":[OSD([sQuery(id+"F0.wireOp",EDGE,"E0"),sQuery(id+"F0.wireOp",EDGE,"R1386e3d-cCkv-oNVg-00Cd-SGYjTnL4WSA1"),sQuery(id+"F0.wireOp",EDGE,"E1"),sQuery(id+"F0.wireOp",EDGE,"E2"),sQuery(id+"F0.wireOp",EDGE,"E3"),sQuery(id+"F0.wireOp",EDGE,"E4"),sQuery(id+"F0.wireOp",EDGE,"E5"),sQuery(id+"F0.wireOp",EDGE,"E6"),sQuery(id+"F0.wireOp",EDGE,"E7"),sQuery(id+"F0.wireOp",EDGE,"E8"),sQuery(id+"F0.wireOp",EDGE,"E9"),sQuery(id+"F0.wireOp",EDGE,"E10"),sQuery(id+"F0.wireOp",EDGE,"E11"),sQuery(id+"F0.wireOp",EDGE,"E12"),sQuery(id+"F0.wireOp",EDGE,"E13"),sQuery(id+"F0.wireOp",EDGE,"ztFaACSw-jiCL-CWtF-o8WQ-KM6RK4UlDnil"),sQuery(id+"F0.wireOp",EDGE,"MWlh78yX-b2Pw-1Exi-RM6v-perESSh9RIu0"),sQuery(id+"F0.wireOp",EDGE,"d3bbb15d-b909-4395-a431-4fd7b84b4cae"),sQuery(id+"F0.wireOp",EDGE,"E14.top"),sQuery(id+"F0.wireOp",EDGE,"E15.top"),sQuery(id+"F0.wireOp",EDGE,"E16.top"),sQuery(id+"F0.wireOp",EDGE,"E17.top"),sQuery(id+"F0.wireOp",EDGE,"E18.top"),sQuery(id+"F0.wireOp",EDGE,"E19.top"),sQuery(id+"F0.wireOp",EDGE,"E20.top"),sQuery(id+"F0.wireOp",EDGE,"E21.top"),sQuery(id+"F0.wireOp",EDGE,"E22.top"),sQuery(id+"F0.wireOp",EDGE,"E23.top"),sQuery(id+"F0.wireOp",EDGE,"E24.top"),sQuery(id+"F0.wireOp",EDGE,"E25.top"),sQuery(id+"F0.wireOp",EDGE,"E26.top"),sQuery(id+"F0.wireOp",EDGE,"E27.top"),sQuery(id+"F0.wireOp",EDGE,"E28.top"),sQuery(id+"F0.wireOp",EDGE,"E29.top"),sQuery(id+"F0.wireOp",EDGE,"E30.top")])]});
            var Q1;
            Q1=makeQuery(id+"F1.opExtrude","SWEPT_EDGE",EDGE,{"disambiguationData":[OSD([sQuery(id+"F0.wireOp",EDGE,"E0"),sQuery(id+"F0.wireOp",EDGE,"E2")])]});
            transform(context, id + "F13", {"entities" : qUnion([Q0]), "transformType" : TransformType.ROTATION, "transformAxis" : qUnion([Q1]), "angle" : 180 * degree, "makeCopy" : false});
        }
        {
            var Q0;
            Q0=makeQuery(id+"F1.opExtrude","CAP_FACE",FACE,{"disambiguationData":[OSD([sQuery(id+"F0.wireOp",EDGE,"E0"),sQuery(id+"F0.wireOp",EDGE,"R1386e3d-cCkv-oNVg-00Cd-SGYjTnL4WSA1"),sQuery(id+"F0.wireOp",EDGE,"E1"),sQuery(id+"F0.wireOp",EDGE,"E2"),sQuery(id+"F0.wireOp",EDGE,"E3"),sQuery(id+"F0.wireOp",EDGE,"E4"),sQuery(id+"F0.wireOp",EDGE,"E5"),sQuery(id+"F0.wireOp",EDGE,"E6"),sQuery(id+"F0.wireOp",EDGE,"E7"),sQuery(id+"F0.wireOp",EDGE,"E8"),sQuery(id+"F0.wireOp",EDGE,"E9"),sQuery(id+"F0.wireOp",EDGE,"E10"),sQuery(id+"F0.wireOp",EDGE,"E11"),sQuery(id+"F0.wireOp",EDGE,"E12"),sQuery(id+"F0.wireOp",EDGE,"E13"),sQuery(id+"F0.wireOp",EDGE,"ztFaACSw-jiCL-CWtF-o8WQ-KM6RK4UlDnil"),sQuery(id+"F0.wireOp",EDGE,"MWlh78yX-b2Pw-1Exi-RM6v-perESSh9RIu0"),sQuery(id+"F0.wireOp",EDGE,"d3bbb15d-b909-4395-a431-4fd7b84b4cae"),sQuery(id+"F0.wireOp",EDGE,"E14.top"),sQuery(id+"F0.wireOp",EDGE,"E15.top"),sQuery(id+"F0.wireOp",EDGE,"E16.top"),sQuery(id+"F0.wireOp",EDGE,"E17.top"),sQuery(id+"F0.wireOp",EDGE,"E18.top"),sQuery(id+"F0.wireOp",EDGE,"E19.top"),sQuery(id+"F0.wireOp",EDGE,"E20.top"),sQuery(id+"F0.wireOp",EDGE,"E21.top"),sQuery(id+"F0.wireOp",EDGE,"E22.top"),sQuery(id+"F0.wireOp",EDGE,"E23.top"),sQuery(id+"F0.wireOp",EDGE,"E24.top"),sQuery(id+"F0.wireOp",EDGE,"E25.top"),sQuery(id+"F0.wireOp",EDGE,"E26.top"),sQuery(id+"F0.wireOp",EDGE,"E27.top"),sQuery(id+"F0.wireOp",EDGE,"E28.top"),sQuery(id+"F0.wireOp",EDGE,"E29.top"),sQuery(id+"F0.wireOp",EDGE,"E30.top")])],"isStart":false});
            var sketch = newSketch(context, id + "F14", { "sketchPlane" : qUnion([Q0])});
            skText(sketch, "E71", { "text": "          Automate Your \nBookkeeping & Accounting \n       at Botkeeper.com", "fontName": "OpenSans-Regular.ttf"});
            const initialGuessF14  = {"E71": [0.03348, 0.02531, 1, 0, 0.00255]};
            skSetInitialGuess(sketch, initialGuessF14);
            skSolve(sketch);
        }
        {
            var Q0;
            Q0 = qSketchRegion(id + "F14", true);
            extrude(context, id + "F15", {"entities" : qUnion([Q0]), "operationType" : NewBodyOperationType.REMOVE, "oppositeDirection" : true, "depth" : 0.25 * mm});
        }
        {
            var Q0;
            {var subQ0=sQuery(id+"F0.wireOp",EDGE,"E6");var subQ1=makeQuery(id+"F1.opExtrude","SWEPT_FACE",FACE,{"disambiguationData":[OSD([subQ0])]});var subQ2=sQuery(id+"F0.wireOp",EDGE,"E7");var subQ4=sQuery(id+"F0.wireOp",EDGE,"E8");var subQ29=sQuery(id+"F0.wireOp",EDGE,"E5");var subQ30=sQuery(id+"F0.wireOp",EDGE,"E4");var subQ34=sQuery(id+"F0.wireOp",EDGE,"E3");var subQ40=sQuery(id+"F0.wireOp",EDGE,"E30.top");var subQ41=sQuery(id+"F0.wireOp",EDGE,"E29.top");var subQ42=sQuery(id+"F0.wireOp",EDGE,"E28.top");var subQ43=sQuery(id+"F0.wireOp",EDGE,"E27.top");var subQ44=sQuery(id+"F0.wireOp",EDGE,"E26.top");var subQ45=sQuery(id+"F0.wireOp",EDGE,"E25.top");var subQ46=sQuery(id+"F0.wireOp",EDGE,"E24.top");var subQ47=sQuery(id+"F0.wireOp",EDGE,"E23.top");var subQ48=sQuery(id+"F0.wireOp",EDGE,"E22.top");var subQ49=sQuery(id+"F0.wireOp",EDGE,"E21.top");var subQ50=sQuery(id+"F0.wireOp",EDGE,"E20.top");var subQ51=sQuery(id+"F0.wireOp",EDGE,"E19.top");var subQ52=sQuery(id+"F0.wireOp",EDGE,"E18.top");var subQ53=sQuery(id+"F0.wireOp",EDGE,"E17.top");var subQ54=sQuery(id+"F0.wireOp",EDGE,"E16.top");var subQ55=sQuery(id+"F0.wireOp",EDGE,"E15.top");var subQ56=sQuery(id+"F0.wireOp",EDGE,"E14.top");var subQ57=sQuery(id+"F0.wireOp",EDGE,"E0");var subQ60=sQuery(id+"F0.wireOp",EDGE,"E31");var subQ61=sQuery(id+"F0.wireOp",EDGE,"E1");var subQ62=sQuery(id+"F0.wireOp",EDGE,"E9");var subQ66=sQuery(id+"F0.wireOp",EDGE,"E11");var subQ69=sQuery(id+"F0.wireOp",EDGE,"E2");var subQ70=makeQuery(id+"F1.opExtrude","SWEPT_FACE",FACE,{"disambiguationData":[OSD([subQ69])]});var subQ95=sQuery(id+"F0.wireOp",EDGE,"E10");var subQ96=sQuery(id+"F0.wireOp",EDGE,"E12");var subQ98=sQuery(id+"F0.wireOp",EDGE,"E13");Q0=makeQuery(id+"F10.boolean.opBoolean","SPLIT",FACE,{"disambiguationData":[TD([subQ1])],"derivedFrom":makeQuery(id+"F8.boolean.opBoolean","SPLIT",FACE,{"disambiguationData":[TD([subQ70])],"derivedFrom":makeQuery(id+"F6.boolean.opBoolean","SPLIT",FACE,{"disambiguationData":[TD([subQ70])],"derivedFrom":makeQuery(id+"F3.boolean.opBoolean","SPLIT",FACE,{"disambiguationData":[TD([subQ70])],"derivedFrom":makeQuery(id+"F1.opExtrude","CAP_FACE",FACE,{"disambiguationData":[OSD([subQ57,subQ61,subQ69,subQ34,subQ30,subQ29,subQ0,subQ2,subQ4,subQ62,subQ95,subQ66,subQ96,subQ98,subQ56,subQ55,subQ54,subQ53,subQ52,subQ51,subQ50,subQ49,subQ48,subQ47,subQ46,subQ45,subQ44,subQ43,subQ42,subQ41,subQ40,subQ60])],"isStart":true})})})})});}
            var sketch = newSketch(context, id + "F16", { "sketchPlane" : qUnion([Q0])});
            skLineSegment(sketch, "E72", {"start": v(10.8, -31.44) * mm, "end": v(7.81, -31.64) * mm});
            skLineSegment(sketch, "E73", {"start": v(7.81, -31.64) * mm, "end": v(8.74, -45.6) * mm});
            skLineSegment(sketch, "E74", {"start": v(8.74, -45.6) * mm, "end": v(20.71, -44.81) * mm});
            skLineSegment(sketch, "E75", {"start": v(20.71, -44.81) * mm, "end": v(20.91, -47.8) * mm});
            skLineSegment(sketch, "E76", {"start": v(20.91, -47.8) * mm, "end": v(5.94, -48.8) * mm});
            skLineSegment(sketch, "E77", {"start": v(5.94, -48.8) * mm, "end": v(4.62, -28.84) * mm});
            skLineSegment(sketch, "E78", {"start": v(10.6, -28.45) * mm, "end": v(4.62, -28.84) * mm});
            skPoint(sketch, "E79.orphan", {"position": v(10.46, -26.19) * mm});
            skPoint(sketch, "E80.0.start.orphan", {"position": v(10.97, -33.94) * mm});
            skSolve(sketch);
        }
        {
            var Q0;
            {var subQ0=sQuery(id+"F16.wireOp",EDGE,"E72");Q0=makeQuery(id+"F16.imprint","IMPRINT",FACE,{"disambiguationData":[TD([[makeQuery(id+"F16.imprint","IMPRINT",EDGE,{"derivedFrom":subQ0}),-1.0]])]});}
            var Q1;
            {var subQ0=sQuery(id+"F0.wireOp",EDGE,"E13");var subQ1=sQuery(id+"F0.wireOp",EDGE,"E12");var subQ2=sQuery(id+"F0.wireOp",EDGE,"E4");var subQ3=sQuery(id+"F0.wireOp",EDGE,"E3");var subQ4=sQuery(id+"F0.wireOp",EDGE,"E31");var subQ5=sQuery(id+"F0.wireOp",EDGE,"E11");var subQ6=sQuery(id+"F0.wireOp",EDGE,"E10");var subQ7=sQuery(id+"F0.wireOp",EDGE,"E9");var subQ8=sQuery(id+"F0.wireOp",EDGE,"E5");var subQ9=sQuery(id+"F0.wireOp",EDGE,"E6");var subQ10=sQuery(id+"F0.wireOp",EDGE,"E8");var subQ11=sQuery(id+"F0.wireOp",EDGE,"E30.top");var subQ12=sQuery(id+"F0.wireOp",EDGE,"E29.top");var subQ13=sQuery(id+"F0.wireOp",EDGE,"E28.top");var subQ14=sQuery(id+"F0.wireOp",EDGE,"E27.top");var subQ15=sQuery(id+"F0.wireOp",EDGE,"E26.top");var subQ16=sQuery(id+"F0.wireOp",EDGE,"E25.top");var subQ17=sQuery(id+"F0.wireOp",EDGE,"E24.top");var subQ18=sQuery(id+"F0.wireOp",EDGE,"E23.top");var subQ19=sQuery(id+"F0.wireOp",EDGE,"E22.top");var subQ20=sQuery(id+"F0.wireOp",EDGE,"E21.top");var subQ21=sQuery(id+"F0.wireOp",EDGE,"E20.top");var subQ22=sQuery(id+"F0.wireOp",EDGE,"E19.top");var subQ23=sQuery(id+"F0.wireOp",EDGE,"E18.top");var subQ24=sQuery(id+"F0.wireOp",EDGE,"E17.top");var subQ25=sQuery(id+"F0.wireOp",EDGE,"E16.top");var subQ26=sQuery(id+"F0.wireOp",EDGE,"E15.top");var subQ27=sQuery(id+"F0.wireOp",EDGE,"E14.top");var subQ28=sQuery(id+"F0.wireOp",EDGE,"E0");var subQ29=sQuery(id+"F0.wireOp",EDGE,"E1");var subQ30=sQuery(id+"F0.wireOp",EDGE,"E7");var subQ31=sQuery(id+"F0.wireOp",EDGE,"E2");Q1=makeQuery(id+"F15.boolean.opBoolean","SPLIT",FACE,{"disambiguationData":[TD([makeQuery(id+"F1.opExtrude","SWEPT_FACE",FACE,{"disambiguationData":[OSD([subQ31])]})])],"derivedFrom":makeQuery(id+"F1.opExtrude","CAP_FACE",FACE,{"disambiguationData":[OSD([subQ28,subQ29,subQ31,subQ3,subQ2,subQ8,subQ9,subQ30,subQ10,subQ7,subQ6,subQ5,subQ1,subQ0,subQ27,subQ26,subQ25,subQ24,subQ23,subQ22,subQ21,subQ20,subQ19,subQ18,subQ17,subQ16,subQ15,subQ14,subQ13,subQ12,subQ11,subQ4])],"isStart":false})});}
            extrude(context, id + "F17", {"entities" : qUnion([Q0]), "operationType" : NewBodyOperationType.ADD, "endBound" : BoundingType.UP_TO_SURFACE, "oppositeDirection" : true, "endBoundEntityFace" : qUnion([Q1]), "depth" : 25 * mm});
        }
        {
            var Q0;
            Q0=makeQuery(id+"F6.boolean.opBoolean","SPLIT",FACE,{"disambiguationData":[TD([makeQuery(id+"F3.boolean.opBoolean","COPY",FACE,{"derivedFrom":makeQuery(id+"F3.opExtrude","SWEPT_FACE",FACE,{"disambiguationData":[OSD([sQuery(id+"F2.wireOp",EDGE,"E34")])]})})])],"derivedFrom":makeQuery(id+"F1.opExtrude","CAP_FACE",FACE,{"disambiguationData":[OSD([sQuery(id+"F0.wireOp",EDGE,"E0"),sQuery(id+"F0.wireOp",EDGE,"E1"),sQuery(id+"F0.wireOp",EDGE,"E2"),sQuery(id+"F0.wireOp",EDGE,"E3"),sQuery(id+"F0.wireOp",EDGE,"E4"),sQuery(id+"F0.wireOp",EDGE,"E5"),sQuery(id+"F0.wireOp",EDGE,"E6"),sQuery(id+"F0.wireOp",EDGE,"E7"),sQuery(id+"F0.wireOp",EDGE,"E8"),sQuery(id+"F0.wireOp",EDGE,"E9"),sQuery(id+"F0.wireOp",EDGE,"E10"),sQuery(id+"F0.wireOp",EDGE,"E11"),sQuery(id+"F0.wireOp",EDGE,"E12"),sQuery(id+"F0.wireOp",EDGE,"E13"),sQuery(id+"F0.wireOp",EDGE,"E14.top"),sQuery(id+"F0.wireOp",EDGE,"E15.top"),sQuery(id+"F0.wireOp",EDGE,"E16.top"),sQuery(id+"F0.wireOp",EDGE,"E17.top"),sQuery(id+"F0.wireOp",EDGE,"E18.top"),sQuery(id+"F0.wireOp",EDGE,"E19.top"),sQuery(id+"F0.wireOp",EDGE,"E20.top"),sQuery(id+"F0.wireOp",EDGE,"E21.top"),sQuery(id+"F0.wireOp",EDGE,"E22.top"),sQuery(id+"F0.wireOp",EDGE,"E23.top"),sQuery(id+"F0.wireOp",EDGE,"E24.top"),sQuery(id+"F0.wireOp",EDGE,"E25.top"),sQuery(id+"F0.wireOp",EDGE,"E26.top"),sQuery(id+"F0.wireOp",EDGE,"E27.top"),sQuery(id+"F0.wireOp",EDGE,"E28.top"),sQuery(id+"F0.wireOp",EDGE,"E29.top"),sQuery(id+"F0.wireOp",EDGE,"E30.top"),sQuery(id+"F0.wireOp",EDGE,"E31")])],"isStart":true})});
            var sketch = newSketch(context, id + "F18", { "sketchPlane" : qUnion([Q0])});
            skFitSpline(sketch, "E81", {"points": [v(71.32, -43.33) * mm, v(72.56, -43.08) * mm, v(74.76, -40.46) * mm, v(76.54, -36.37) * mm, v(77.26, -31.31) * mm, v(76.49, -28.5) * mm, v(74.58, -26.6) * mm, v(72.61, -25.85) * mm, v(70.5, -26.38) * mm, v(68.17, -27.16) * mm, v(65.26, -27.49) * mm, v(62.25, -27.47) * mm, v(59.5, -26.74) * mm, v(57.35, -26.1) * mm, v(55.7, -26.3) * mm, v(53.44, -27.56) * mm, v(52.07, -29.86) * mm, v(52, -33.5) * mm, v(53, -37.2) * mm, v(54.82, -41.15) * mm, v(56.68, -43.22) * mm, v(57.96, -43.48) * mm, v(59.33, -43.14) * mm, v(61.35, -41.59) * mm, v(62.48, -40.68) * mm, v(64.68, -40.16) * mm, v(67.11, -40.71) * mm, v(68.38, -41.6) * mm, v(69.3, -42.54) * mm, v(70.5, -43.18) * mm, v(71.32, -43.33) * mm]});
            skSolve(sketch);
        }
        {
            var Q0;
            Q0 = qSketchRegion(id + "F18", true);
            extrude(context, id + "F19", {"entities" : qUnion([Q0]), "operationType" : NewBodyOperationType.REMOVE, "oppositeDirection" : true, "depth" : 25 * mm});
        }
    });
